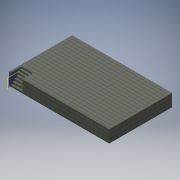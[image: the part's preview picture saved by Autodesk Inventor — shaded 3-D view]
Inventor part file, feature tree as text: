
AUTODESK INVENTOR PART (.ipt)
format: ipt  version: 2017 (Build 210142000, 142)  size: 200,704 bytes
history: native  units: mm
features: extrude x4, sketch x4, projected_geometry x3, plane x1
ambient origin geometry x8: Origin, YZ Plane, XZ Plane, XY Plane, X Axis, Y Axis, Z Axis, Center Point
bodies: Volumenkörper1 (feature_tree)
feature tree (12):
  extrude  "Extrusion1"  Depth=7150.0mm
  plane  "Arbeitsebene1"
  extrude  "Extrusion3"  [1 undecoded]
  extrude  "Extrusion4"  Depth=200.0mm
  extrude  "Extrusion5"  Depth=200.0mm
  sketch  "Skizze1"  dims[d0=11360.0mm d1=7150.0mm]
  sketch  "Skizze2"  dims[d2=1400.0mm d3=0.0mm d4=-200.0mm]
  projected_geometry  "Projizierte Kontur1"
  sketch  "Skizze4"  dims[d5=200.0mm d6=200.0mm]
  projected_geometry  "Projizierte Kontur3"
  sketch  "Skizze5"  dims[d7=200.0mm d8=200.0mm d9=200.0mm d10=200.0mm d11=200.0mm d12=200.0mm d15=200.0mm d16=200.0mm d17=200.0mm d18=200.0mm d19=1280.0mm d20=0.0mm d41=200.0mm d42=200.0mm d43=200.0mm d44=200.0mm d45=200.0mm d46=1300.0mm d47=2300.0mm d48=0.0mm d49=200.0mm d50=200.0mm d51=6620.0mm d52=3400.0mm d53=970.0mm d54=1600.0mm d55=200.0mm d56=4050.0mm d57=200.0mm d58=2300.0mm d59=0.0mm d60=3850.0mm d61=200.0mm]
  projected_geometry  "Projizierte Kontur4"
note: 1 required parameter value undecoded (feature->parameter linkage not recoverable at this tier; creation-order binding heuristic only, values carry confidence <= 0.55)
